# Revit family: Vierteaguas Y. C-1
name_source: partatom
category: Modelos genéricos
units: mm (PartAtom-declared; Revit-internal decimal feet)

## family parameters
Compartido = No
Corte con vacíos al cargar = No
Cota de conector redondo = Diámetro de uso
Puede alojar armadura = No
Punto de cálculo de habitación = No
Se basa en plano de trabajo = No
Siempre vertical = No
Tipo de pieza = Normal

## types (7) — shared parameters
Descripción = Pieza de hormigón polímero con anclaje de acero inoxidable.
Fabricante = ULMA Architectural Solutions
Material = Hormigón polímero STONEO. Color C-1
URL = https://www.ulmaarchitectural.com
zero-valued in all types: Elevación por defecto

## per-type parameters (varying)
| type | Ancho | Ancho total | Modelo |
| Y16 | 160 mm  [stored 0.524934 ft] | 185 mm  [stored 0.606955 ft] | Vierteaguas Y16 |
| Y18 | 180 mm  [stored 0.590551 ft] | 205 mm  [stored 0.672572 ft] | Vierteaguas Y18 |
| Y20 | 200 mm  [stored 0.656168 ft] | 225 mm  [stored 0.738189 ft] | Vierteaguas Y20 |
| Y24 | 240 mm  [stored 0.787402 ft] | 265 mm  [stored 0.869423 ft] | Vierteaguas Y24 |
| Y26 | 260 mm  [stored 0.853018 ft] | 285 mm  [stored 0.935039 ft] | Vierteaguas Y26 |
| Y28 | 280 mm  [stored 0.918635 ft] | 305 mm  [stored 1.00066 ft] | Vierteaguas Y28 |
| Y22 | 220 mm  [stored 0.721785 ft] | 245 mm  [stored 0.803806 ft] | Vierteaguas Y22 |

note: column(s) folded — value = type name in every type: Código de montaje

note: [stored X ft] marks values corroborated as IEEE doubles in the binary element streams (Revit-internal decimal feet)
